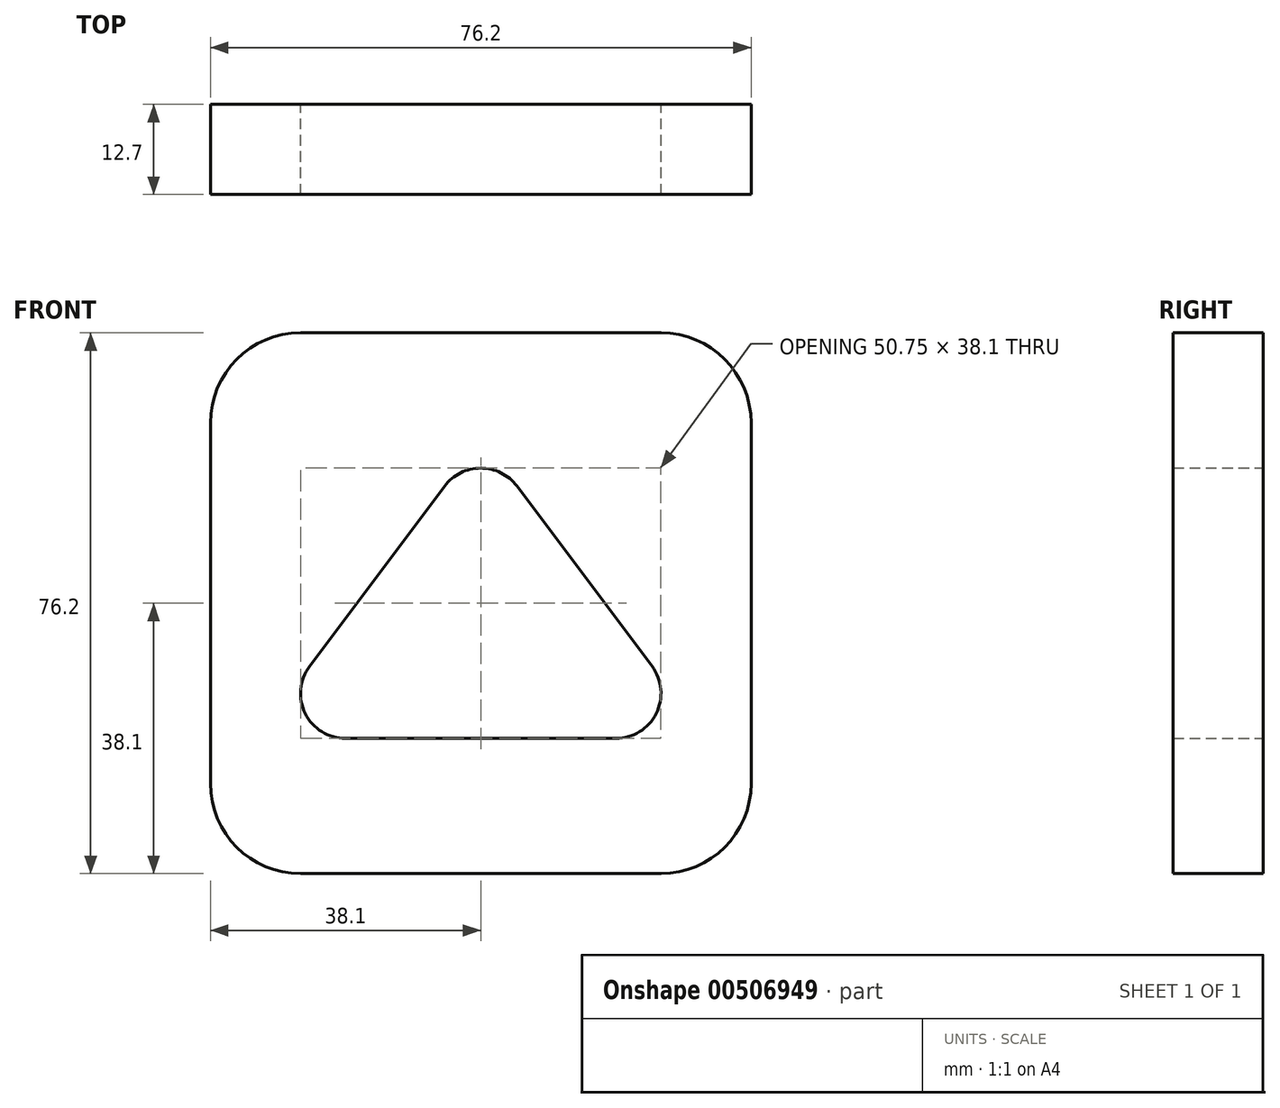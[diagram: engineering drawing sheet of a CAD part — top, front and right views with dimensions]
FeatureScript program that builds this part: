
annotation { "Feature Type Name" : "Feature", "Feature Type Description" : "" }
export const myFeature = defineFeature(function(context is Context, id is Id, definition is map)
    precondition{}
    {
        {
            var Q0;
            Q0=qCreatedBy(makeId("Front.planeOp"),FACE);
            var sketch = newSketch(context, id + "F0", { "sketchPlane" : qUnion([Q0])});
            skLineSegment(sketch, "E0", {"start": v(12.7, 0) * mm, "end": v(63.5, 0) * mm});
            skLineSegment(sketch, "E1", {"start": v(76.2, 12.7) * mm, "end": v(76.2, 63.5) * mm});
            skLineSegment(sketch, "E2", {"start": v(63.5, 76.2) * mm, "end": v(12.7, 76.2) * mm});
            skLineSegment(sketch, "E3", {"start": v(0, 63.5) * mm, "end": v(0, 0) * mm});
            skLineSegment(sketch, "E4", {"start": v(0, 63.5) * mm, "end": v(0, 12.7) * mm});
            skArc(sketch, "E5", {"start": v(13.97, 29.21) * mm, "mid": v(13.37, 22.56) * mm, "end": v(19.05, 19.05) * mm});
            skArc(sketch, "E6", {"start": v(57.15, 19.05) * mm, "mid": v(62.83, 22.56) * mm, "end": v(62.23, 29.21) * mm});
            skArc(sketch, "E7", {"start": v(43.18, 54.6) * mm, "mid": v(38.1, 57.15) * mm, "end": v(33.02, 54.6) * mm});
            skLineSegment(sketch, "E8", {"start": v(33.02, 54.6) * mm, "end": v(13.97, 29.21) * mm});
            skLineSegment(sketch, "E9", {"start": v(43.18, 54.6) * mm, "end": v(62.23, 29.21) * mm});
            skLineSegment(sketch, "E10", {"start": v(19.05, 19.05) * mm, "end": v(57.15, 19.05) * mm});
            skArc(sketch, "E11", {"start": v(12.7, 76.2) * mm, "mid": v(3.72, 72.48) * mm, "end": v(0, 63.5) * mm});
            skArc(sketch, "E12", {"start": v(76.2, 63.5) * mm, "mid": v(72.48, 72.48) * mm, "end": v(63.5, 76.2) * mm});
            skArc(sketch, "E13", {"start": v(0, 12.7) * mm, "mid": v(3.72, 3.72) * mm, "end": v(12.7, 0) * mm});
            skArc(sketch, "E14", {"start": v(63.5, 0) * mm, "mid": v(72.48, 3.72) * mm, "end": v(76.2, 12.7) * mm});
            skSolve(sketch);
        }
        {
            var Q0;
            Q0=makeQuery(id+"F0.imprint","IMPRINT",FACE,{"disambiguationData":[TD([[makeQuery(id+"F0.imprint","IMPRINT",EDGE,{"derivedFrom":sQuery(id+"F0.wireOp",EDGE,"E0")}),1.0]])]});
            extrude(context, id + "F1", {"entities" : qUnion([Q0]), "depth" : 12.7 * mm});
        }
    });
